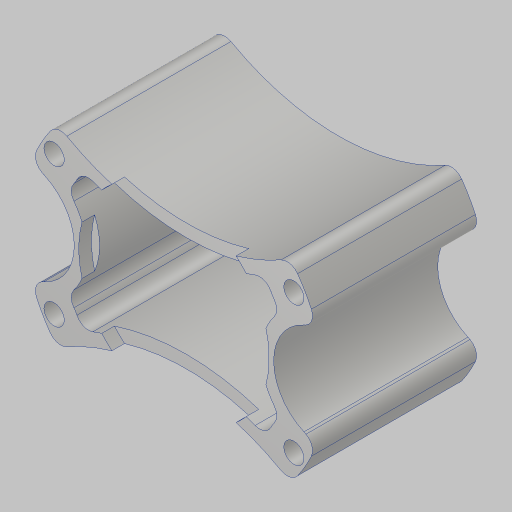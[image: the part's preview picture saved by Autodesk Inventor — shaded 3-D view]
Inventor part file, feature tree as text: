
AUTODESK INVENTOR PART (.ipt)
format: ipt  version: 2023.5 (Build 275446000, 446)  size: 243,200 bytes
history: native  units: in
note: dims shown in document units (in); Inventor stores cm internally (conversion verified against a paired STEP export)
features: sketch x2, extrude x2, fillet x1, hole x1
ambient origin geometry x8: Origin, YZ Plane, XZ Plane, XY Plane, X Axis, Y Axis, Z Axis, Center Point
bodies: Solid1 (feature_tree)
feature tree (6):
  sketch  "Sketch1"  dims[d0=2.375in d1=1.375in d2=0.5in]
  extrude  "Extrusion1"  Depth=1.375in
  fillet  "Fillet1"  Radius=0.5in
  hole  "Hole1"  [1 undecoded]
  extrude  "Extrusion2"  Depth=0.5in
  sketch  "Sketch3"  dims[d3=0.5in d4=0.5in d5=0.5in d6=1.25in d7=0.5in d8=0.5in d9=0.125in d10=0.125in d11=1.625in d12=0.0in d13=0.125in d14=0.201in d15=0.75in d16=0.385in d17=0.25in d18=0.5635in d19=1.0in d20=0.8108in d21=1.885in d22=0.125in d23=0.0in d24=0.125in d25=0.125in d26=0.125in d27=3.0in d28=1.0in]
note: 1 required parameter value undecoded (feature->parameter linkage not recoverable at this tier; creation-order binding heuristic only, values carry confidence <= 0.55)
